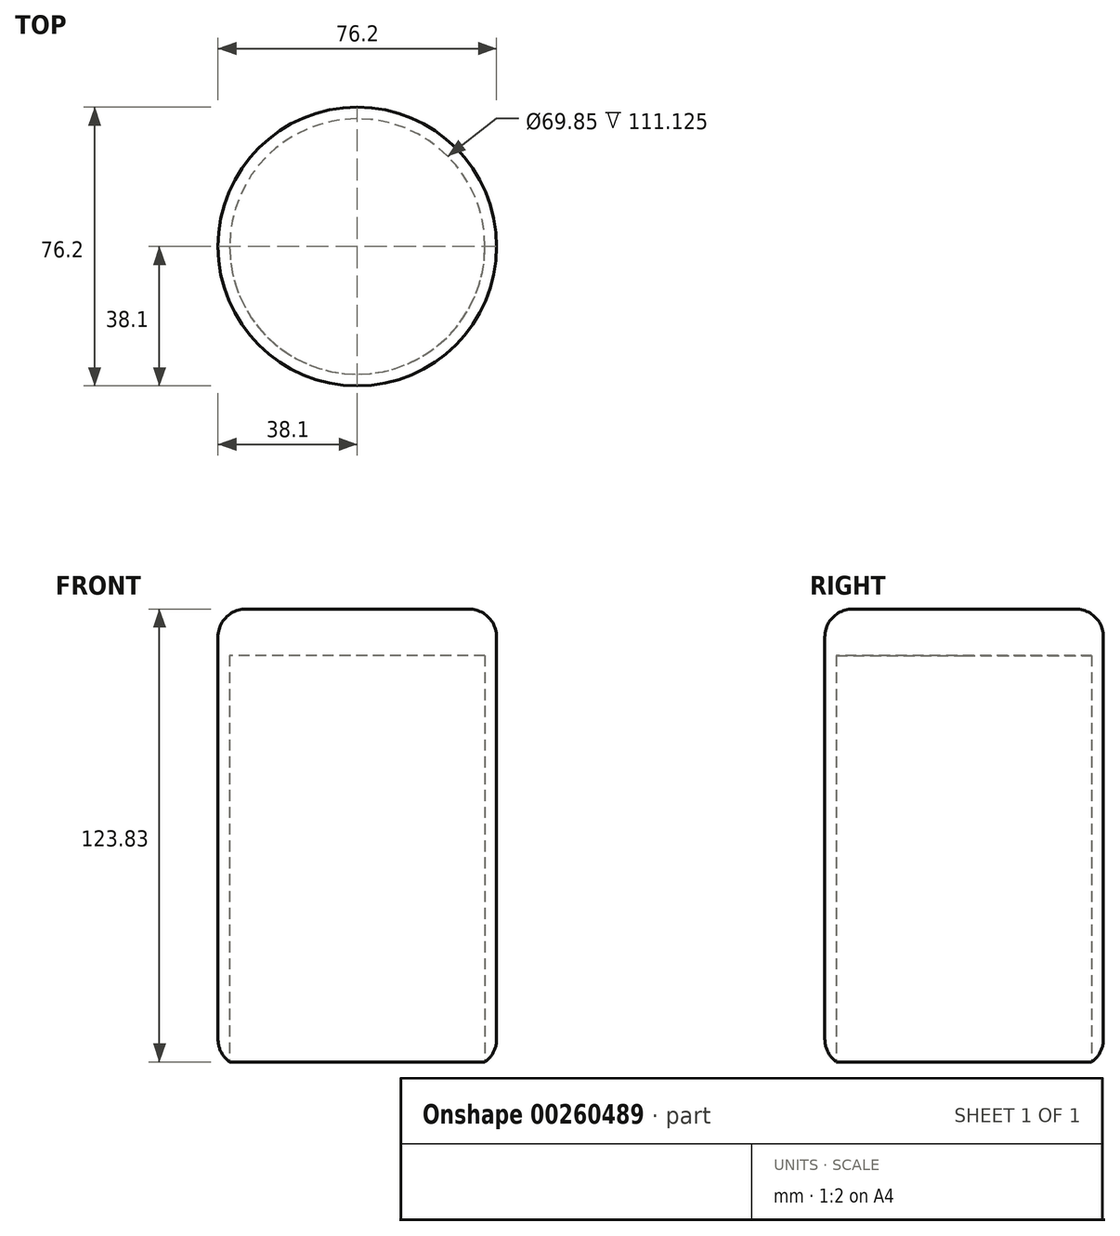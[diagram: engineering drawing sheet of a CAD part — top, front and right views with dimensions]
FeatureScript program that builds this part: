
annotation { "Feature Type Name" : "Feature", "Feature Type Description" : "" }
export const myFeature = defineFeature(function(context is Context, id is Id, definition is map)
    precondition{}
    {
        {
            var Q0;
            Q0=qCreatedBy(makeId("Top.planeOp"),FACE);
            var sketch = newSketch(context, id + "F0", { "sketchPlane" : qUnion([Q0])});
            skCircle(sketch, "E0", {"center": v(0, 0) * mm, "radius": 38.1 * mm});
            skSolve(sketch);
        }
        {
            var Q0;
            Q0 = qSketchRegion(id + "F0", true);
            extrude(context, id + "F1", {"entities" : qUnion([Q0]), "depth" : 123.82 * mm});
        }
        {
            var Q0;
            Q0=qCreatedBy(makeId("Top.planeOp"),FACE);
            var sketch = newSketch(context, id + "F2", { "sketchPlane" : qUnion([Q0])});
            skCircle(sketch, "E1", {"center": v(0, 0) * mm, "radius": 34.93 * mm});
            skSolve(sketch);
        }
        {
            var Q0;
            Q0 = qSketchRegion(id + "F2", true);
            extrude(context, id + "F3", {"entities" : qUnion([Q0]), "operationType" : NewBodyOperationType.REMOVE, "depth" : 111.12 * mm});
        }
        {
            var Q0;
            Q0=makeQuery(id+"F1.opExtrude","CAP_EDGE",EDGE,{"disambiguationData":[OSD([sQuery(id+"F0.wireOp",EDGE,"E0")])],"isStart":true});
            fillet(context, id + "F4", {"entities" : qUnion([Q0]), "radius" : 7.62 * mm, "tangentPropagation" : true, "allowEdgeOverflow" : false});
        }
        {
            var Q0;
            Q0=makeQuery(id+"F1.opExtrude","CAP_EDGE",EDGE,{"disambiguationData":[OSD([sQuery(id+"F0.wireOp",EDGE,"E0")])],"isStart":false});
            fillet(context, id + "F5", {"entities" : qUnion([Q0]), "radius" : 7.62 * mm, "tangentPropagation" : true, "allowEdgeOverflow" : false});
        }
    });
